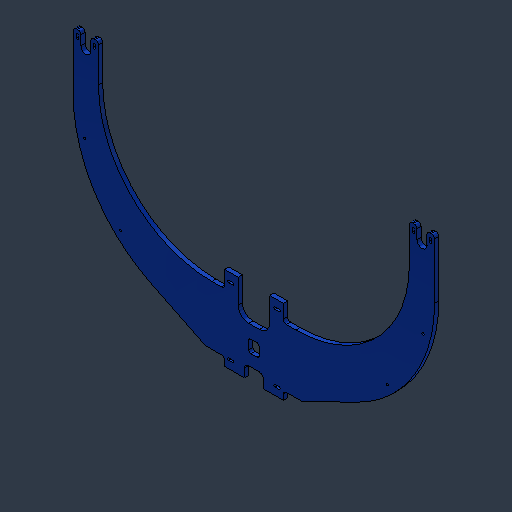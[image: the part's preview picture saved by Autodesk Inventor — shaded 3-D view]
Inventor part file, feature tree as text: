
AUTODESK INVENTOR PART (.ipt)
format: ipt  version: 2024.3 (Build 283343000, 343)  size: 161,280 bytes
history: native  units: mm (DEFAULTED — no unit token found)
features: fillet x1
ambient origin geometry x8: Origin, YZ Plane, XZ Plane, XY Plane, X Axis, Y Axis, Z Axis, Center Point
bodies: Solid1 (feature_tree)
feature tree (1):
  fillet  "Fillet5"  [1 undecoded]
note: 1 required parameter value undecoded (feature->parameter linkage not recoverable at this tier; creation-order binding heuristic only, values carry confidence <= 0.55)
